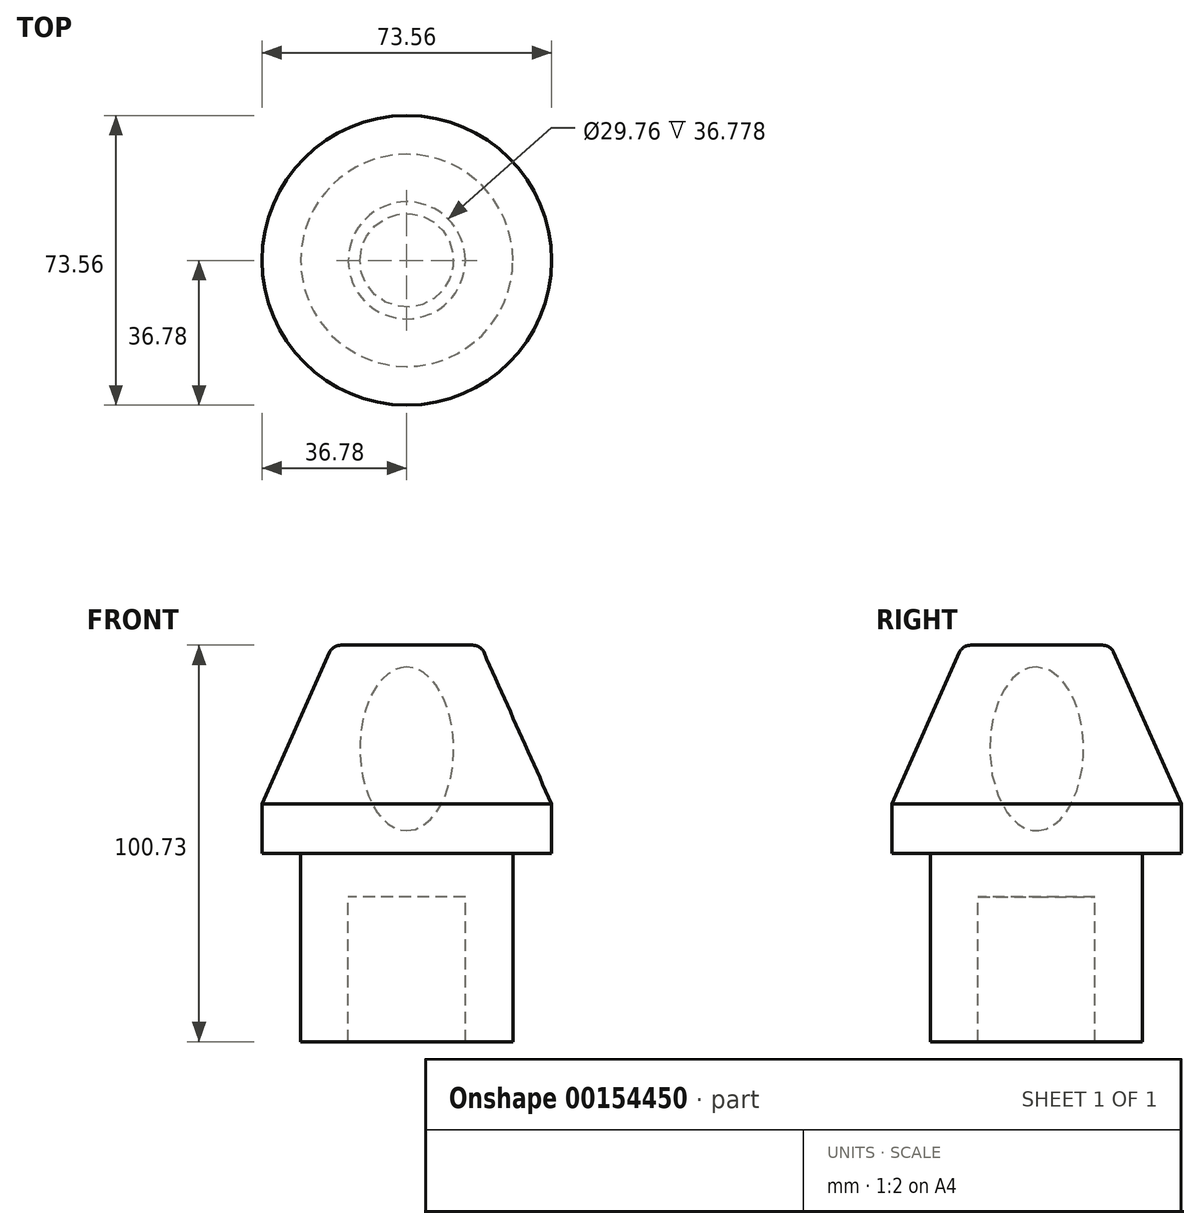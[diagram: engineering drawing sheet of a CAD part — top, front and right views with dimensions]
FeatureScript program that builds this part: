
annotation { "Feature Type Name" : "Feature", "Feature Type Description" : "" }
export const myFeature = defineFeature(function(context is Context, id is Id, definition is map)
    precondition{}
    {
        {
            var Q0;
            Q0=qCreatedBy(makeId("Front.planeOp"),FACE);
            var sketch = newSketch(context, id + "F0", { "sketchPlane" : qUnion([Q0])});
            skLineSegment(sketch, "E0", {"start": v(-14.88, -47.87) * mm, "end": v(-26.95, -47.87) * mm});
            skLineSegment(sketch, "E1", {"start": v(-26.95, -47.87) * mm, "end": v(-26.95, 0) * mm});
            skLineSegment(sketch, "E2", {"start": v(-26.95, 0) * mm, "end": v(-36.78, 0) * mm});
            skLineSegment(sketch, "E3", {"start": v(-36.78, 0) * mm, "end": v(-36.78, 12.5) * mm});
            skLineSegment(sketch, "E4", {"start": v(-36.78, 12.5) * mm, "end": v(-19.57, 51.08) * mm});
            skLineSegment(sketch, "E5", {"start": v(-16.83, 52.86) * mm, "end": v(0, 52.86) * mm});
            skLineSegment(sketch, "E6", {"start": v(-14.88, -47.87) * mm, "end": v(-14.88, -11.09) * mm});
            skLineSegment(sketch, "E7", {"start": v(-14.88, -11.09) * mm, "end": v(0, -11.09) * mm});
            skPoint(sketch, "E8.visualSharp", {"position": v(-18.78, 52.86) * mm});
            skArc(sketch, "E8.filletArc", {"start": v(-16.83, 52.86) * mm, "mid": v(-18.46, 52.38) * mm, "end": v(-19.57, 51.08) * mm});
            skLineSegment(sketch, "E9", {"start": v(0, 52.86) * mm, "end": v(0, -11.09) * mm});
            skEllipse(sketch, "E10", {"center": v(0, 26.53) * mm, "majorRadius": 20.78 * mm, "minorRadius": 11.9 * mm, "majorAxis": v(0, -1)});
            skSolve(sketch);
        }
        {
            var Q0;
            Q0=makeQuery(id+"F0.imprint","IMPRINT",FACE,{"disambiguationData":[TD([[makeQuery(id+"F0.imprint","IMPRINT",EDGE,{"derivedFrom":sQuery(id+"F0.wireOp",EDGE,"E0")}),-1.0]])]});
            var Q1;
            Q1=sQuery(id+"F0.wireOp",EDGE,"E9");
            revolve(context, id + "F1", {"entities" : qUnion([Q0]), "axis" : qUnion([Q1]), "revolveType" : RevolveType.FULL});
        }
    });
